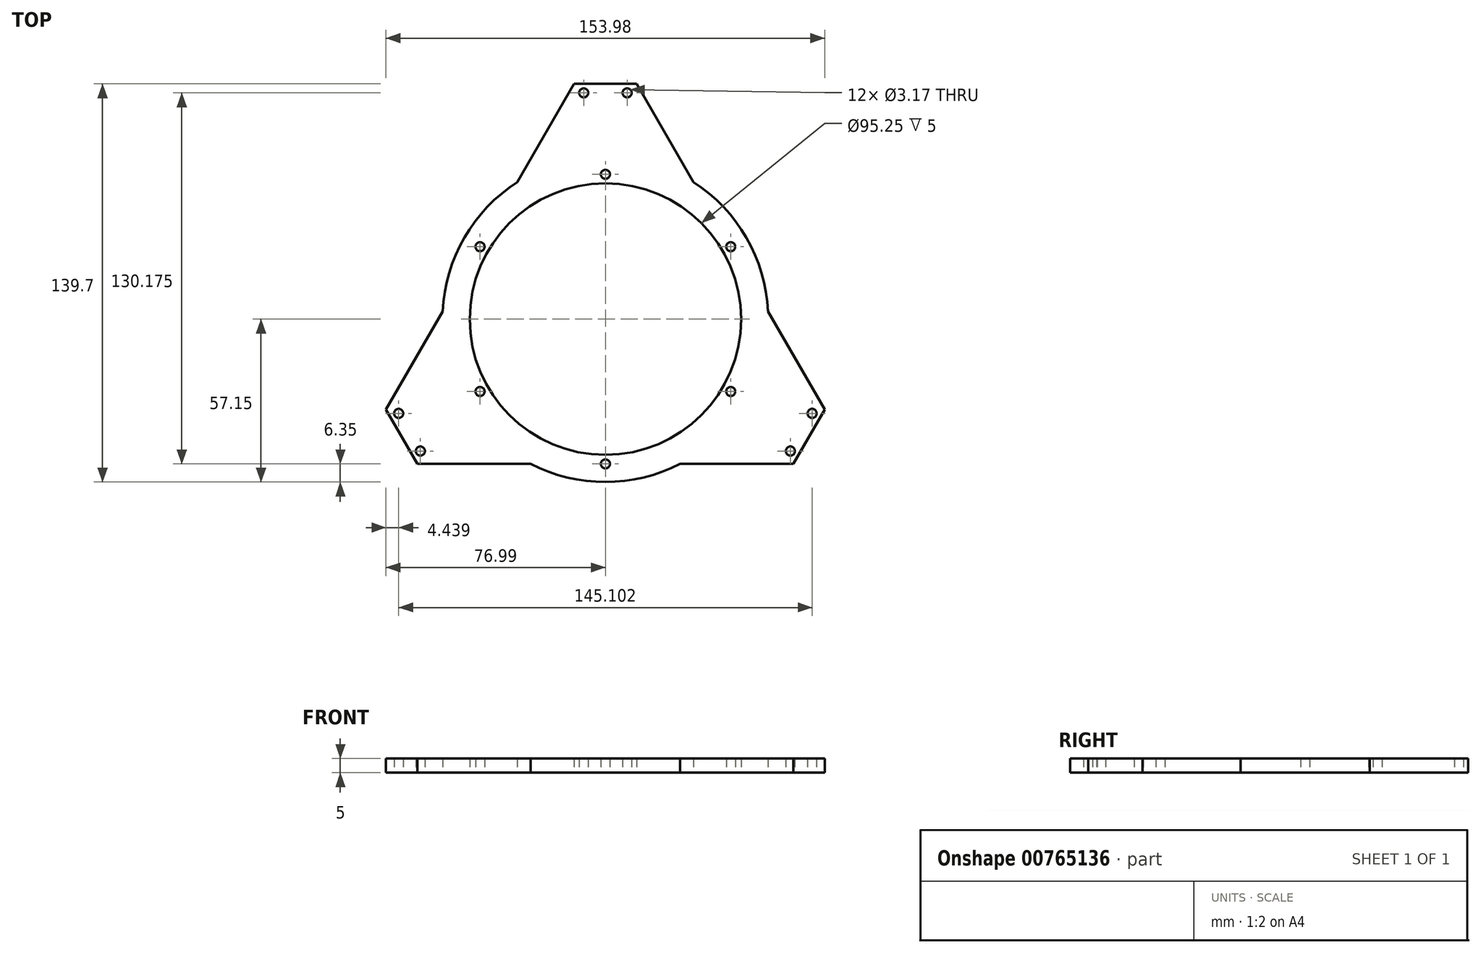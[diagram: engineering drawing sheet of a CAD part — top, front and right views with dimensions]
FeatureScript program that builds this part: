
annotation { "Feature Type Name" : "Feature", "Feature Type Description" : "" }
export const myFeature = defineFeature(function(context is Context, id is Id, definition is map)
    precondition{}
    {
        {
            var Q0;
            Q0=qCreatedBy(makeId("Top.planeOp"),FACE);
            var sketch = newSketch(context, id + "F0", { "sketchPlane" : qUnion([Q0])});
            skCircle(sketch, "E0.cCircle", {"center": v(0, 0) * mm, "radius": 101.6 * mm, "construction": true});
            skLineSegment(sketch, "E0.0", {"start": v(0, 101.6) * mm, "end": v(30.9, 48.07) * mm});
            skLineSegment(sketch, "E0.1", {"start": v(87.99, -50.8) * mm, "end": v(26.18, -50.8) * mm});
            skLineSegment(sketch, "E0.2", {"start": v(-87.99, -50.8) * mm, "end": v(-57.08, 2.73) * mm});
            skLineSegment(sketch, "E1", {"start": v(-87.99, -50.8) * mm, "end": v(0, 0) * mm});
            skLineSegment(sketch, "E2", {"start": v(0, 0) * mm, "end": v(87.99, -50.8) * mm});
            skLineSegment(sketch, "E3", {"start": v(0, 0) * mm, "end": v(0, 101.6) * mm});
            skPoint(sketch, "E4", {"position": v(0, 82.55) * mm});
            skPoint(sketch, "E5", {"position": v(-71.5, -41.27) * mm});
            skPoint(sketch, "E6", {"position": v(71.5, -41.27) * mm});
            skCircle(sketch, "E7", {"center": v(0, 0) * mm, "radius": 47.63 * mm});
            skPoint(sketch, "E8", {"position": v(-44, -25.4) * mm});
            skPoint(sketch, "E9", {"position": v(44, -25.4) * mm});
            skPoint(sketch, "E10", {"position": v(0, 50.8) * mm});
            skLineSegment(sketch, "E11", {"start": v(-30.9, 48.07) * mm, "end": v(0, 101.6) * mm});
            skArc(sketch, "E12", {"start": v(-30.9, 48.07) * mm, "mid": v(-49.5, 28.57) * mm, "end": v(-57.08, 2.73) * mm});
            skLineSegment(sketch, "E13", {"start": v(57.08, 2.73) * mm, "end": v(87.99, -50.8) * mm});
            skArc(sketch, "E14", {"start": v(57.08, 2.73) * mm, "mid": v(49.5, 28.58) * mm, "end": v(30.9, 48.07) * mm});
            skArc(sketch, "E15", {"start": v(-26.18, -50.8) * mm, "mid": v(0, -57.15) * mm, "end": v(26.18, -50.8) * mm});
            skLineSegment(sketch, "E16", {"start": v(-26.18, -50.8) * mm, "end": v(-87.99, -50.8) * mm});
            skCircle(sketch, "E17", {"center": v(-44, -25.4) * mm, "radius": 1.59 * mm});
            skCircle(sketch, "E18", {"center": v(44, -25.4) * mm, "radius": 1.59 * mm});
            skCircle(sketch, "E19", {"center": v(0, 50.8) * mm, "radius": 1.59 * mm});
            skPoint(sketch, "E20", {"position": v(-44, 25.4) * mm});
            skPoint(sketch, "E21", {"position": v(0, -50.8) * mm});
            skPoint(sketch, "E22", {"position": v(44, 25.4) * mm});
            skCircle(sketch, "E23", {"center": v(-44, 25.4) * mm, "radius": 1.59 * mm});
            skCircle(sketch, "E24", {"center": v(44, 25.4) * mm, "radius": 1.59 * mm});
            skCircle(sketch, "E25", {"center": v(0, -50.8) * mm, "radius": 1.59 * mm});
            skPoint(sketch, "E26", {"position": v(-7.62, 79.38) * mm});
            skPoint(sketch, "E26.positionSnap0", {"position": v(-15.45, 74.84) * mm});
            skPoint(sketch, "E27", {"position": v(7.62, 79.38) * mm});
            skPoint(sketch, "E27.positionSnap0", {"position": v(15.45, 74.84) * mm});
            skLineSegment(sketch, "E28", {"start": v(0, 82.55) * mm, "end": v(-11, 82.55) * mm});
            skLineSegment(sketch, "E29", {"start": v(0, 82.55) * mm, "end": v(11, 82.55) * mm});
            skCircle(sketch, "E30", {"center": v(-7.62, 79.38) * mm, "radius": 1.59 * mm});
            skCircle(sketch, "E31", {"center": v(7.62, 79.38) * mm, "radius": 1.59 * mm});
            skLineSegment(sketch, "E32.1.0", {"start": v(-71.5, -41.27) * mm, "end": v(-66, -50.8) * mm});
            skLineSegment(sketch, "E32.1.1", {"start": v(-71.5, -41.27) * mm, "end": v(-76.99, -31.75) * mm});
            skCircle(sketch, "E32.1.2", {"center": v(-72.55, -33.09) * mm, "radius": 1.59 * mm});
            skCircle(sketch, "E32.1.3", {"center": v(-64.93, -46.29) * mm, "radius": 1.59 * mm});
            skLineSegment(sketch, "E32.2.0", {"start": v(71.5, -41.28) * mm, "end": v(76.99, -31.75) * mm});
            skLineSegment(sketch, "E32.2.1", {"start": v(71.5, -41.28) * mm, "end": v(66, -50.8) * mm});
            skCircle(sketch, "E32.2.2", {"center": v(64.93, -46.29) * mm, "radius": 1.59 * mm});
            skCircle(sketch, "E32.2.3", {"center": v(72.55, -33.09) * mm, "radius": 1.59 * mm});
            skSolve(sketch);
        }
        {
            var Q0;
            {var subQ8=sQuery(id+"F0.wireOp",EDGE,"E12");Q0=makeQuery(id+"F0.imprint","IMPRINT",FACE,{"disambiguationData":[TD([[makeQuery(id+"F0.imprint","IMPRINT",EDGE,{"derivedFrom":subQ8}),1.0]])]});}
            var Q1;
            {var subQ0=sQuery(id+"F0.wireOp",EDGE,"E14");Q1=makeQuery(id+"F0.imprint","IMPRINT",FACE,{"disambiguationData":[TD([[makeQuery(id+"F0.imprint","IMPRINT",EDGE,{"derivedFrom":subQ0}),1.0]])]});}
            var Q2;
            {var subQ6=sQuery(id+"F0.wireOp",EDGE,"E15");Q2=makeQuery(id+"F0.imprint","IMPRINT",FACE,{"disambiguationData":[TD([[makeQuery(id+"F0.imprint","IMPRINT",EDGE,{"derivedFrom":subQ6}),1.0]])]});}
            extrude(context, id + "F1", {"entities" : qUnion([Q0, Q1, Q2]), "depth" : 5 * mm, "offsetDistance" : 25.4 * mm});
        }
    });
